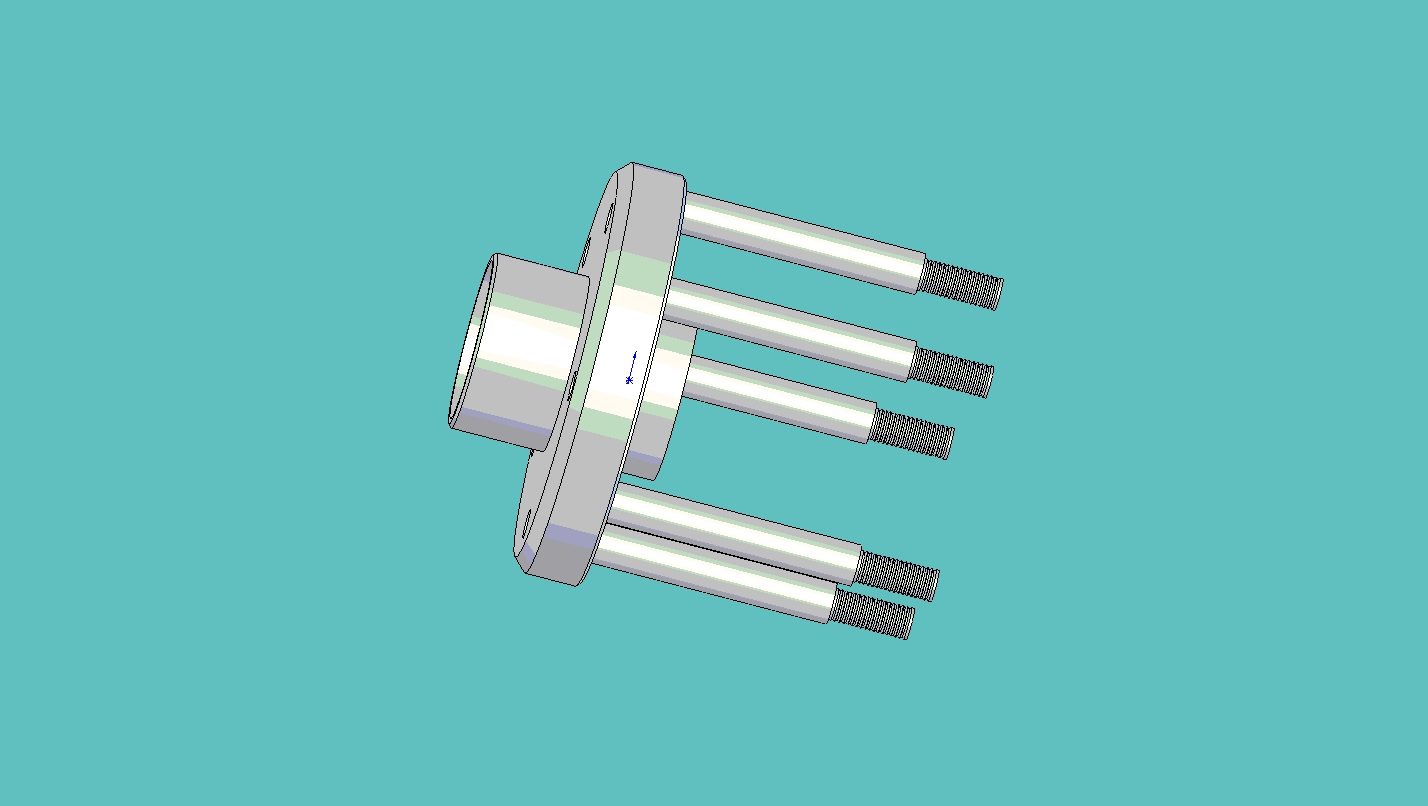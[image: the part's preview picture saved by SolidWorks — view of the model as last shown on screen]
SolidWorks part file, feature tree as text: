
SOLIDWORKS PART (.sldprt)
format: sldprt  version: not decoded by parser v0  size: 1,025,024 bytes
history: native  units: mm
features: sketch x10, cut_extrude x5, extrude x4, chamfer x4, pattern_circular x2, material x1, plane x1, cut_revolve x1, pattern_linear x1 (+13 scaffold rows collapsed)
feature tree (42):
  scaffold x13  (default folders/planes/origin — collapsed)
  material  "Material <not specified>"
  sketch  "Sketch1"  dims[D1=165.1mm]
  extrude  "Extrude1"  Depth=1.27mm
  sketch  "Sketch2"  dims[D1=158.75mm]
  cut_extrude  "Cut-Extrude1"  Depth=2.54mm
  sketch  "Sketch3"  dims[D1=~70.445004mm]
  chamfer  "Chamfer1"  Distance=2.54mm Angle=45deg
  sketch  "Sketch8"  dims[D1=16.51mm D2=~70.192131mm]
  extrude  "Extrude5"  Depth=101.6mm
  extrude  "Extrude6"  Depth=17.78mm
  sketch  "Sketch9"
  cut_extrude  "Cut-Extrude2"  Depth=15.24mm
  sketch  "Sketch10"
  cut_extrude  "Cut-Extrude3"  Depth=25.4mm
  chamfer  "Chamfer4"  Distance=1.27mm Angle=45deg
  sketch  "Sketch11"
  cut_extrude  "Cut-Extrude4"  [1 undecoded]
  sketch  "Sketch12"
  cut_extrude  "Cut-Extrude5"  [1 undecoded]
  sketch  "Sketch13"  dims[D1=12.7mm]
  plane  "Plane2"  Offset=21.59mm
  chamfer  "Chamfer5"  Distance=5.08mm Angle=45deg
  chamfer  "Chamfer6"  Distance=1.27mm Angle=45deg
  extrude  "Extrude7"  Depth=31.75mm
  pattern_circular  "CirPattern1"  Count=5 Angle=360deg
  sketch  "Sketch14"  dims[D1=1.5748mm]
  cut_revolve  "Cut-Revolve1"  Angle=360deg
  pattern_linear  "LPattern2"  Count1=17 Count2=1 Spacing1=1.74mm Spacing2=50mm
  pattern_circular  "CirPattern2"  Count=5 Angle=360deg
decode coverage: 21 of 27 modeling features carry decoded parameters
note: ~ marks probable driven/reference dimensions
note: 2 parameter values undecoded
note: suppression state not decoded; provenance and decode notes live in map.json
